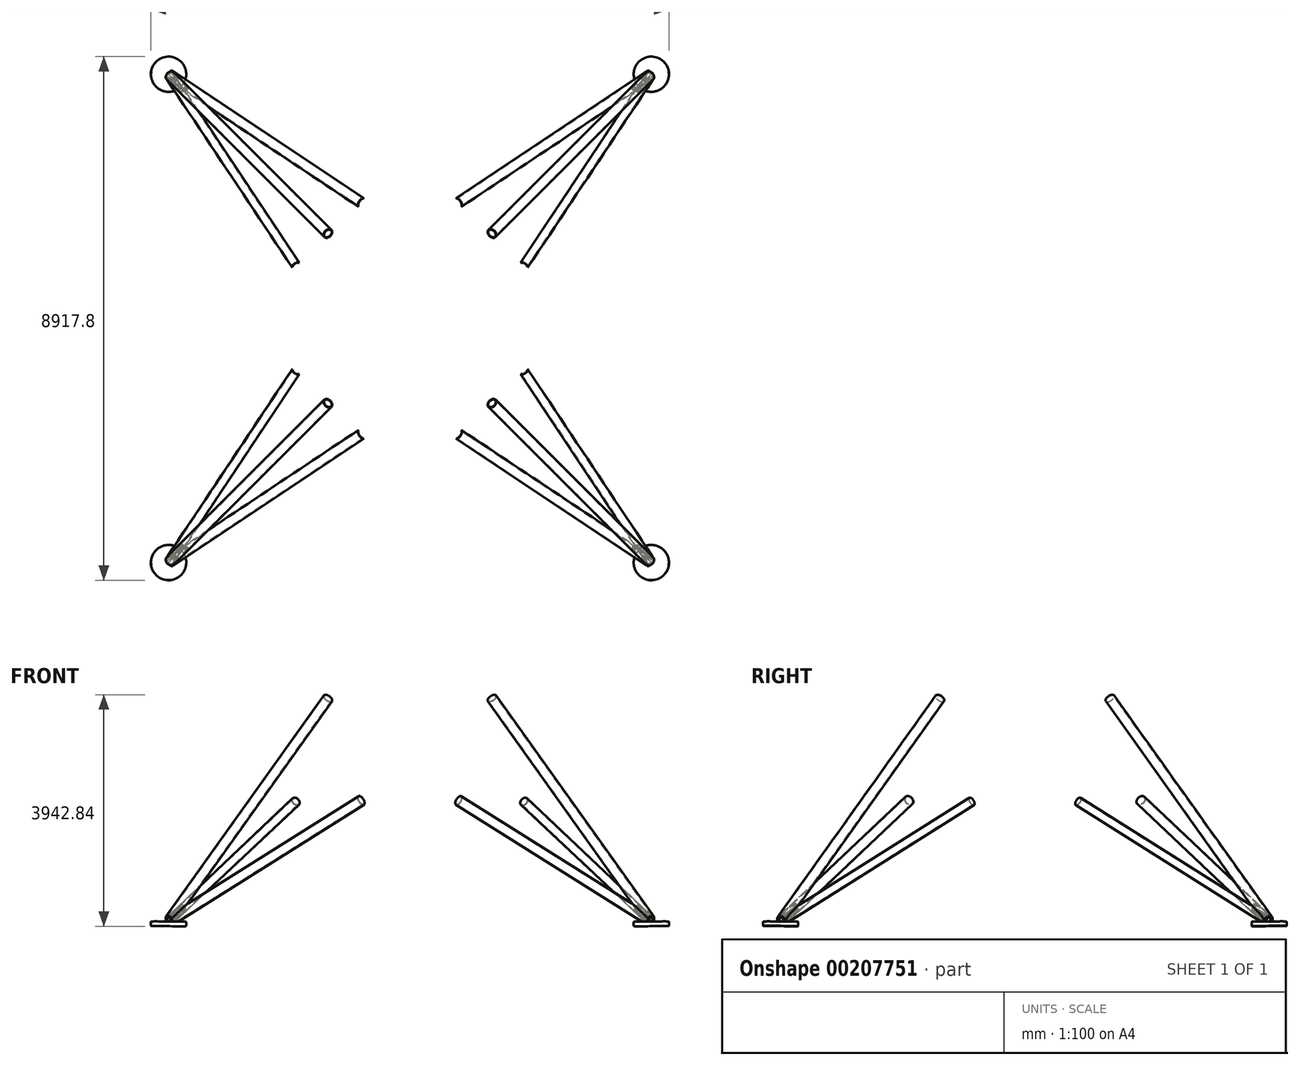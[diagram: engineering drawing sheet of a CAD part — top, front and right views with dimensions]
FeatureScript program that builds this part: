
annotation { "Feature Type Name" : "Feature", "Feature Type Description" : "" }
export const myFeature = defineFeature(function(context is Context, id is Id, definition is map)
    precondition{}
    {
        {
            var Q0;
            Q0=qCreatedBy(makeId("Top.planeOp"),FACE);
            cPlane(context, id + "F0", {"entities" : qUnion([Q0]), "cplaneType" : CPlaneType.OFFSET, "offset" : (1778 + 483) * mm, "width" : 150 * mm, "height" : 150 * mm});
        }
        {
            var Q0;
            Q0=qCreatedBy(id+"F0.planeOp",FACE);
            var sketch = newSketch(context, id + "F1", { "sketchPlane" : qUnion([Q0])});
            skLineSegment(sketch, "E0", {"start": v(-750, 1900) * mm, "end": v(-1850, 800) * mm, "construction": true});
            skLineSegment(sketch, "E1", {"start": v(-1850, 800) * mm, "end": v(-1850, -800) * mm, "construction": true});
            skLineSegment(sketch, "E2", {"start": v(-1850, -800) * mm, "end": v(-750, -1900) * mm, "construction": true});
            skLineSegment(sketch, "E3", {"start": v(-750, -1900) * mm, "end": v(750, -1900) * mm, "construction": true});
            skLineSegment(sketch, "E4", {"start": v(750, -1900) * mm, "end": v(1850, -800) * mm, "construction": true});
            skLineSegment(sketch, "E5", {"start": v(1850, -800) * mm, "end": v(1850, 800) * mm, "construction": true});
            skLineSegment(sketch, "E6", {"start": v(1850, 800) * mm, "end": v(750, 1900) * mm, "construction": true});
            skLineSegment(sketch, "E7", {"start": v(750, 1900) * mm, "end": v(-750, 1900) * mm, "construction": true});
            skSolve(sketch);
        }
        {
            var Q0;
            Q0=qCreatedBy(id+"F0.planeOp",FACE);
            var sketch = newSketch(context, id + "F2", { "sketchPlane" : qUnion([Q0])});
            skLineSegment(sketch, "E8.0", {"start": v(813.64, -1963.64) * mm, "end": v(1913.64, -863.64) * mm, "construction": true});
            skLineSegment(sketch, "E9", {"start": v(1913.64, -863.64) * mm, "end": v(1850, -800) * mm, "construction": true});
            skLineSegment(sketch, "E10", {"start": v(813.64, -1963.64) * mm, "end": v(750, -1900) * mm, "construction": true});
            skSolve(sketch);
        }
        {
            var Q0;
            Q0=sQuery(id+"F2.wireOp",EDGE,"E8.0");
            cPlane(context, id + "F3", {"entities" : qUnion([Q0]), "cplaneType" : CPlaneType.LINE_ANGLE, "offset" : 25 * mm, "angle" : 151.9 * degree, "oppositeDirection" : true, "width" : 150 * mm, "height" : 150 * mm});
        }
        {
            var Q0;
            Q0=qCreatedBy(id+"F3.planeOp",FACE);
            var sketch = newSketch(context, id + "F4", { "sketchPlane" : qUnion([Q0])});
            skPoint(sketch, "E11", {"position": v(3325.7, 3823.54) * mm});
            skLineSegment(sketch, "E12", {"start": v(414.98, 523.88) * mm, "end": v(3325.7, 3823.54) * mm, "construction": true});
            skLineSegment(sketch, "E13", {"start": v(3325.7, 3823.54) * mm, "end": v(-168.32, 1038.43) * mm, "construction": true});
            skLineSegment(sketch, "E14", {"start": v(3325.7, 3823.54) * mm, "end": v(998.29, 9.33) * mm, "construction": true});
            skSolve(sketch);
        }
        {
            var Q0;
            Q0=qCreatedBy(id+"F3.planeOp",FACE);
            var sketch = newSketch(context, id + "F5", { "sketchPlane" : qUnion([Q0])});
            skLineSegment(sketch, "E15", {"start": v(964.8, 98.44) * mm, "end": v(975.04, 92.2) * mm});
            skLineSegment(sketch, "E16", {"start": v(975.04, 92.2) * mm, "end": v(3256.3, 3830.74) * mm});
            skLineSegment(sketch, "E17", {"start": v(3256.3, 3830.74) * mm, "end": v(3246.05, 3837) * mm});
            skLineSegment(sketch, "E18", {"start": v(3246.05, 3837) * mm, "end": v(964.8, 98.44) * mm});
            skSolve(sketch);
        }
        {
            var Q0;
            Q0=makeQuery(id+"F5.imprint","IMPRINT",FACE,{"disambiguationData":[TD([[makeQuery(id+"F5.imprint","IMPRINT",EDGE,{"derivedFrom":sQuery(id+"F5.wireOp",EDGE,"E15")}),1.0]])]});
            var Q1;
            Q1=sQuery(id+"F4.wireOp",EDGE,"E14");
            revolve(context, id + "F6", {"surfaceOperationType" : NewSurfaceOperationType.NEW, "entities" : qUnion([Q0]), "axis" : qUnion([Q1]), "revolveType" : RevolveType.FULL});
        }
        {
            var Q0;
            Q0=qCreatedBy(id+"F3.planeOp",FACE);
            var sketch = newSketch(context, id + "F7", { "sketchPlane" : qUnion([Q0])});
            skLineSegment(sketch, "E19", {"start": v(-198, 1110.68) * mm, "end": v(3255.5, 3863.49) * mm});
            skLineSegment(sketch, "E20", {"start": v(3255.5, 3863.49) * mm, "end": v(3248.01, 3872.87) * mm});
            skLineSegment(sketch, "E21", {"start": v(3248.01, 3872.87) * mm, "end": v(-205.48, 1120.06) * mm});
            skLineSegment(sketch, "E22", {"start": v(-205.48, 1120.06) * mm, "end": v(-198, 1110.68) * mm});
            skSolve(sketch);
        }
        {
            var Q0;
            Q0=makeQuery(id+"F7.imprint","IMPRINT",FACE,{"disambiguationData":[TD([[makeQuery(id+"F7.imprint","IMPRINT",EDGE,{"derivedFrom":sQuery(id+"F7.wireOp",EDGE,"E19")}),1.0]])]});
            var Q1;
            Q1=sQuery(id+"F4.wireOp",EDGE,"E13");
            revolve(context, id + "F8", {"operationType" : NewBodyOperationType.ADD, "surfaceOperationType" : NewSurfaceOperationType.NEW, "entities" : qUnion([Q0]), "axis" : qUnion([Q1]), "revolveType" : RevolveType.FULL});
        }
        {
            var Q0;
            Q0=qCreatedBy(id+"F3.planeOp",FACE);
            var sketch = newSketch(context, id + "F9", { "sketchPlane" : qUnion([Q0])});
            skLineSegment(sketch, "E23", {"start": v(3325.7, 3823.54) * mm, "end": v(3550.68, 3625.08) * mm, "construction": true});
            skSolve(sketch);
        }
        {
            var Q0;
            Q0=sQuery(id+"F9.wireOp",EDGE,"E23");
            var Q1;
            Q1=qCreatedBy(id+"F3.planeOp",FACE);
            cPlane(context, id + "F10", {"entities" : qUnion([Q0, Q1]), "cplaneType" : CPlaneType.LINE_ANGLE, "offset" : 25 * mm, "angle" : 28.9 * degree, "oppositeDirection" : true, "width" : 150 * mm, "height" : 150 * mm});
        }
        {
            var Q0;
            Q0=qCreatedBy(id+"F10.planeOp",FACE);
            var sketch = newSketch(context, id + "F11", { "sketchPlane" : qUnion([Q0])});
            skCircle(sketch, "E24", {"center": v(4109.43, -4159.83) * mm, "radius": 300 * mm});
            skSolve(sketch);
        }
        {
            var Q0;
            Q0=makeQuery(id+"F11.imprint","IMPRINT",FACE,{"disambiguationData":[TD([[makeQuery(id+"F11.imprint","IMPRINT",EDGE,{"derivedFrom":sQuery(id+"F11.wireOp",EDGE,"E24")}),1.0]])]});
            extrude(context, id + "F12", {"entities" : qUnion([Q0]), "operationType" : NewBodyOperationType.ADD, "oppositeDirection" : true, "depth" : 75 * mm, "offsetDistance" : 25 * mm});
        }
        {
            var Q0;
            Q0=sQuery(id+"F4.wireOp",EDGE,"E12");
            var Q1;
            Q1=qCreatedBy(id+"F0.planeOp",FACE);
            cPlane(context, id + "F13", {"entities" : qUnion([Q0, Q1]), "cplaneType" : CPlaneType.LINE_ANGLE, "offset" : 25 * mm, "angle" : 90 * degree, "width" : 150 * mm, "height" : 150 * mm});
        }
        {
            var Q0;
            Q0=qCreatedBy(id+"F13.planeOp",FACE);
            var sketch = newSketch(context, id + "F14", { "sketchPlane" : qUnion([Q0])});
            skLineSegment(sketch, "E25", {"start": v(-1963.83, 2261) * mm, "end": v(-1938.7, 4060.82) * mm, "construction": true});
            skLineSegment(sketch, "E26", {"start": v(-1938.7, 4060.82) * mm, "end": v(-5845.2, 188.55) * mm, "construction": true});
            skLineSegment(sketch, "E27", {"start": v(-1956.92, 3937.16) * mm, "end": v(-5756.88, 170.48) * mm});
            skLineSegment(sketch, "E28", {"start": v(-5756.88, 170.48) * mm, "end": v(-5748.43, 161.96) * mm});
            skLineSegment(sketch, "E29", {"start": v(-5748.43, 161.96) * mm, "end": v(-1948.47, 3928.64) * mm});
            skLineSegment(sketch, "E30", {"start": v(-1948.47, 3928.64) * mm, "end": v(-1956.92, 3937.16) * mm});
            skSolve(sketch);
        }
        {
            var Q0;
            Q0=makeQuery(id+"F14.imprint","IMPRINT",FACE,{"disambiguationData":[TD([[makeQuery(id+"F14.imprint","IMPRINT",EDGE,{"derivedFrom":sQuery(id+"F14.wireOp",EDGE,"E27")}),1.0]])]});
            var Q1;
            Q1=sQuery(id+"F14.wireOp",EDGE,"E26");
            revolve(context, id + "F15", {"operationType" : NewBodyOperationType.ADD, "surfaceOperationType" : NewSurfaceOperationType.NEW, "entities" : qUnion([Q0]), "axis" : qUnion([Q1]), "revolveType" : RevolveType.FULL});
        }
        {
            var Q0;
            Q0=makeQuery(id+"F6.opRevolve","SWEPT_BODY",BODY,{"disambiguationData":[OSD([sQuery(id+"F5.wireOp",EDGE,"E15"),sQuery(id+"F5.wireOp",EDGE,"E16"),sQuery(id+"F5.wireOp",EDGE,"E17"),sQuery(id+"F5.wireOp",EDGE,"E18")])]});
            var Q1;
            Q1=qCreatedBy(makeId("Front.planeOp"),FACE);
            mirror(context, id + "F16", {"entities" : qUnion([Q0]), "mirrorPlane" : qUnion([Q1])});
        }
        {
            var Q0;
            Q0=makeQuery(id+"F6.opRevolve","SWEPT_BODY",BODY,{"disambiguationData":[OSD([sQuery(id+"F5.wireOp",EDGE,"E15"),sQuery(id+"F5.wireOp",EDGE,"E16"),sQuery(id+"F5.wireOp",EDGE,"E17"),sQuery(id+"F5.wireOp",EDGE,"E18")])]});
            var Q1;
            Q1=makeQuery(id+"F16.opPattern","COPY",BODY,{"derivedFrom":makeQuery(id+"F6.opRevolve","SWEPT_BODY",BODY,{"disambiguationData":[OSD([sQuery(id+"F5.wireOp",EDGE,"E15"),sQuery(id+"F5.wireOp",EDGE,"E16"),sQuery(id+"F5.wireOp",EDGE,"E17"),sQuery(id+"F5.wireOp",EDGE,"E18")])]}),"instanceName":"1"});
            var Q2;
            Q2=qCreatedBy(makeId("Right.planeOp"),FACE);
            mirror(context, id + "F17", {"entities" : qUnion([Q0, Q1]), "mirrorPlane" : qUnion([Q2])});
        }
    });
